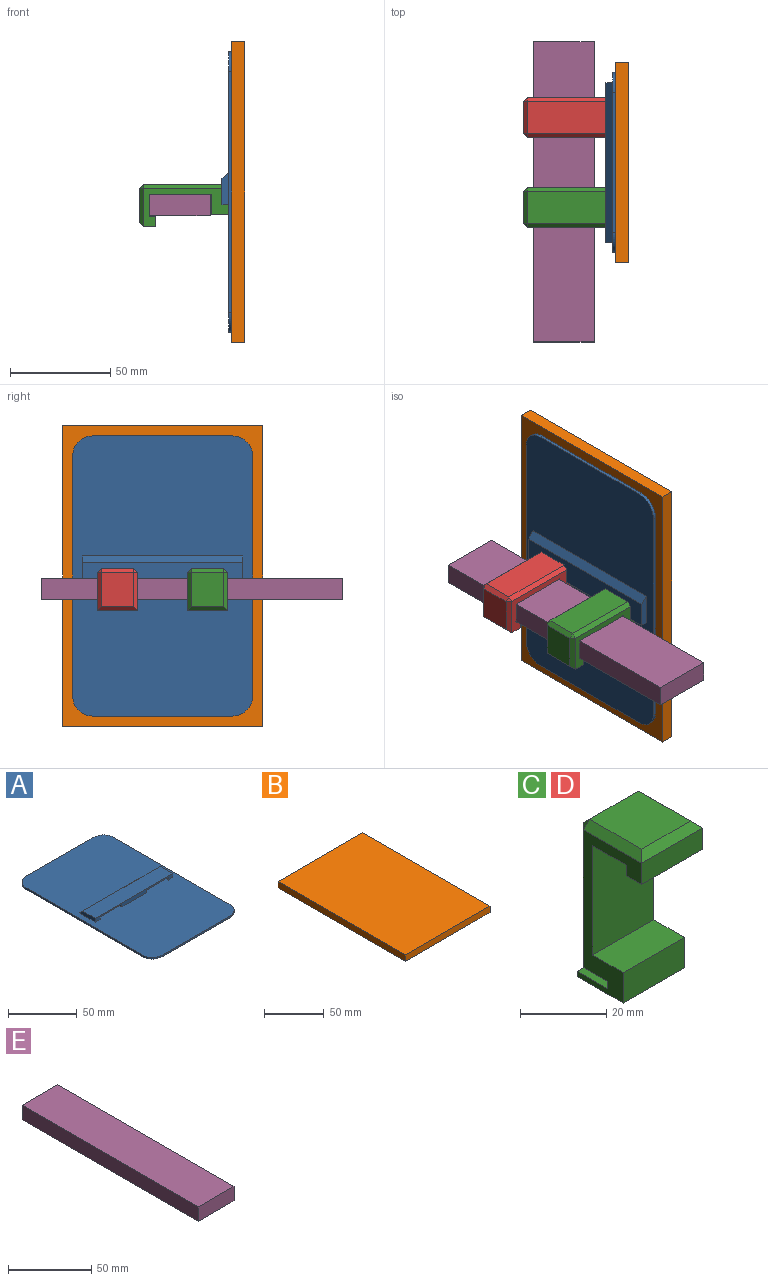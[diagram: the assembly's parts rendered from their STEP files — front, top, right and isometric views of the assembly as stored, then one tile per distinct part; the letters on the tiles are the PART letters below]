
ASSEMBLY  parts=5 mates=5
PART A: 23 faces, bbox 90x140x4.8 mm
  f0: plane 22.5x10mm, normal (0,0,-1), area 225mm2, adj f1,f16,f20,f22
  f1: plane 22.5x2.1mm, normal (0,-1,0), area 47.3mm2, adj f0,f2,f20,f22
  f2: plane 140x90mm, normal (0,0,1), area 11660.2mm2, adj f1,f4,f5,f6,f7,f8,f10,f11
  f3: plane 22.5x10mm, normal (0,0,-1), area 225mm2, adj f4,f16,f19,f21
  f4: plane 22.5x2.1mm, normal (0,-1,0), area 47.3mm2, adj f2,f3,f19,f21
  f5: plane 120x1.5mm, normal (-1,0,0), area 180mm2, adj f2,f9,f10,f13
  f6: plane 70x1.5mm, normal (0,-1,0), area 105mm2, adj f2,f9,f10,f11
  f7: plane 120x1.5mm, normal (1,0,0), area 180mm2, adj f2,f9,f11,f12
  f8: plane 70x1.5mm, normal (0,1,0), area 105mm2, adj f2,f9,f12,f13
  f9: plane 140x90mm, normal (0,0,-1), area 12514.2mm2, adj f5,f6,f7,f8,f10,f11,f12,f13
  f10: cylinder r=10mm len=10mm, axis (0,0,-1), area 23.6mm2, adj f2,f5,f6,f9
  f11: cylinder r=10mm len=10mm, axis (0,0,1), area 23.6mm2, adj f2,f6,f7,f9
  f12: cylinder r=10mm len=10mm, axis (0,0,-1), area 23.6mm2, adj f2,f7,f8,f9
  f13: cylinder r=10mm len=10mm, axis (0,0,1), area 23.6mm2, adj f2,f5,f8,f9
  f14: plane 80x3.3mm, normal (0,0.71,0.71), area 373.4mm2, adj f2,f15,f17,f18
  f15: plane 80x13mm, normal (0,0,1), area 1040mm2, adj f14,f16,f17,f18
  f16: plane 80x3.3mm, normal (0,-1,0), area 169.5mm2, adj f0,f2,f3,f15,f17,f18,f19,f20
  f17: plane 16.3x3.3mm, normal (1,0,0), area 48.3mm2, adj f2,f14,f15,f16
  f18: plane 16.3x3.3mm, normal (-1,0,0), area 48.3mm2, adj f2,f14,f15,f16
  f19: plane 10x2.1mm, normal (-1,0,0), area 21mm2, adj f2,f3,f4,f16
  f20: plane 10x2.1mm, normal (1,0,0), area 21mm2, adj f0,f1,f2,f16
  f21: plane 10x2.1mm, normal (1,0,0), area 21mm2, adj f2,f3,f4,f16
  f22: plane 10x2.1mm, normal (-1,0,0), area 21mm2, adj f0,f1,f2,f16
PART B: 6 faces, bbox 100x150x6.6 mm
  f0: plane 100x6.6mm, normal (0,1,0), area 660mm2, adj f1,f3,f4,f5
  f1: plane 150x6.6mm, normal (-1,0,0), area 990mm2, adj f0,f2,f4,f5
  f2: plane 100x6.6mm, normal (0,-1,0), area 660mm2, adj f1,f3,f4,f5
  f3: plane 150x6.6mm, normal (1,0,0), area 990mm2, adj f0,f2,f4,f5
  f4: plane 150x100mm, normal (0,0,1), area 15000mm2, adj f0,f1,f2,f3
  f5: plane 150x100mm, normal (0,0,-1), area 15000mm2, adj f0,f1,f2,f3
PART C: 24 faces, bbox 20x21x44.6 mm
  f0: plane 20x15mm, normal (0,0,-1), area 300mm2, adj f1,f13,f14,f15
  f1: plane 20x1.5mm, normal (0,1,0), area 30mm2, adj f0,f2,f14,f15
  f2: plane 20x10mm, normal (0,0,1), area 200mm2, adj f1,f3,f14,f15
  f3: plane 20x2.1mm, normal (0,1,0), area 42mm2, adj f2,f4,f14,f15
  f4: plane 20x10mm, normal (0,0,-1), area 196mm2, adj f3,f5,f14,f15,f16,f17
  f5: plane 39x16mm, normal (0,1,0), area 624mm2, adj f4,f16,f17,f18
  f6: plane 17x16mm, normal (0,0,1), area 272mm2, adj f18,f21,f22,f23
  f7: plane 20x6mm, normal (0,-1,0), area 120mm2, adj f8,f14,f15,f23
  f8: plane 20x5mm, normal (0,0,-1), area 100mm2, adj f7,f9,f14,f15
  f9: plane 20x3mm, normal (0,1,0), area 60mm2, adj f8,f10,f14,f15
  f10: plane 20x11mm, normal (0,0,-1), area 220mm2, adj f9,f11,f14,f15
  f11: plane 31x20mm, normal (0,-1,0), area 620mm2, adj f10,f12,f14,f15
  f12: plane 20x10mm, normal (0,0,1), area 200mm2, adj f11,f13,f14,f15
  f13: plane 20x8.6mm, normal (0,-1,0), area 172mm2, adj f0,f12,f14,f15
  f14: plane 42.6x21mm, normal (1,0,0), area 263mm2, adj f0,f1,f2,f3,f4,f7,f8,f9
  f15: plane 42.6x21mm, normal (-1,0,0), area 263mm2, adj f0,f1,f2,f3,f4,f7,f8,f9
  f16: plane 39x2mm, normal (0.71,0.71,0), area 110.3mm2, adj f4,f5,f14,f19
  f17: plane 39x2mm, normal (-0.71,0.71,0), area 110.3mm2, adj f4,f5,f15,f20
  f18: plane 16x2mm, normal (0,0.71,0.71), area 45.3mm2, adj f5,f6,f19,f20
  f19: plane 2x2mm, normal (0.58,0.58,0.58), area 3.5mm2, adj f16,f18,f21
  f20: plane 2x2mm, normal (-0.58,0.58,0.58), area 3.5mm2, adj f17,f18,f22
  f21: plane 19x2mm, normal (0.71,0,0.71), area 50.9mm2, adj f6,f14,f19,f23
  f22: plane 19x2mm, normal (-0.71,0,0.71), area 50.9mm2, adj f6,f15,f20,f23
  f23: plane 20x2mm, normal (0,-0.71,0.71), area 50.9mm2, adj f6,f7,f21,f22
PART D: same geometry as C
PART E: 6 faces, bbox 30.5x150x10.7 mm
  f0: plane 30.45x10.65mm, normal (0,1,0), area 324.3mm2, adj f1,f3,f4,f5
  f1: plane 150x10.65mm, normal (-1,0,0), area 1597.5mm2, adj f0,f2,f4,f5
  f2: plane 30.45x10.65mm, normal (0,-1,0), area 324.3mm2, adj f1,f3,f4,f5
  f3: plane 150x10.65mm, normal (1,0,0), area 1597.5mm2, adj f0,f2,f4,f5
  f4: plane 150x30.45mm, normal (0,0,1), area 4567.5mm2, adj f0,f1,f2,f3
  f5: plane 150x30.45mm, normal (0,0,-1), area 4567.5mm2, adj f0,f1,f2,f3
PLACE A rot(axis=(0.58,-0.58,-0.58),120deg) t=(93.93,2.99,66.94)mm
PLACE B rot(axis=(-0.58,-0.58,0.58),120deg) t=(93.93,2.99,66.94)mm
PLACE C rot(axis=(0.58,-0.58,-0.58),120deg) t=(93.93,-9.51,66.94)mm
PLACE D rot(axis=(0.58,-0.58,-0.58),120deg) t=(93.93,35.49,66.94)mm
PLACE E t=(64.75,-11.67,54.99)mm
MATE fastened B.f4 <-> A.f9  axis (-1,0,0) through (90.63,2.99,66.94)mm
MATE fastened A.f4 <-> C.f1  axis (0,0,-1) through (89.13,-9.51,70.64)mm
MATE fastened A.f1 <-> D.f1  axis (0,0,-1) through (89.13,15.49,70.64)mm
MATE slider D.f14 <-> E.f2  axis (0,-1,0) through (49.53,15.49,65.64)mm
MATE slider C.f14 <-> E.f2  axis (0,-1,0) through (49.53,-29.51,65.64)mm
